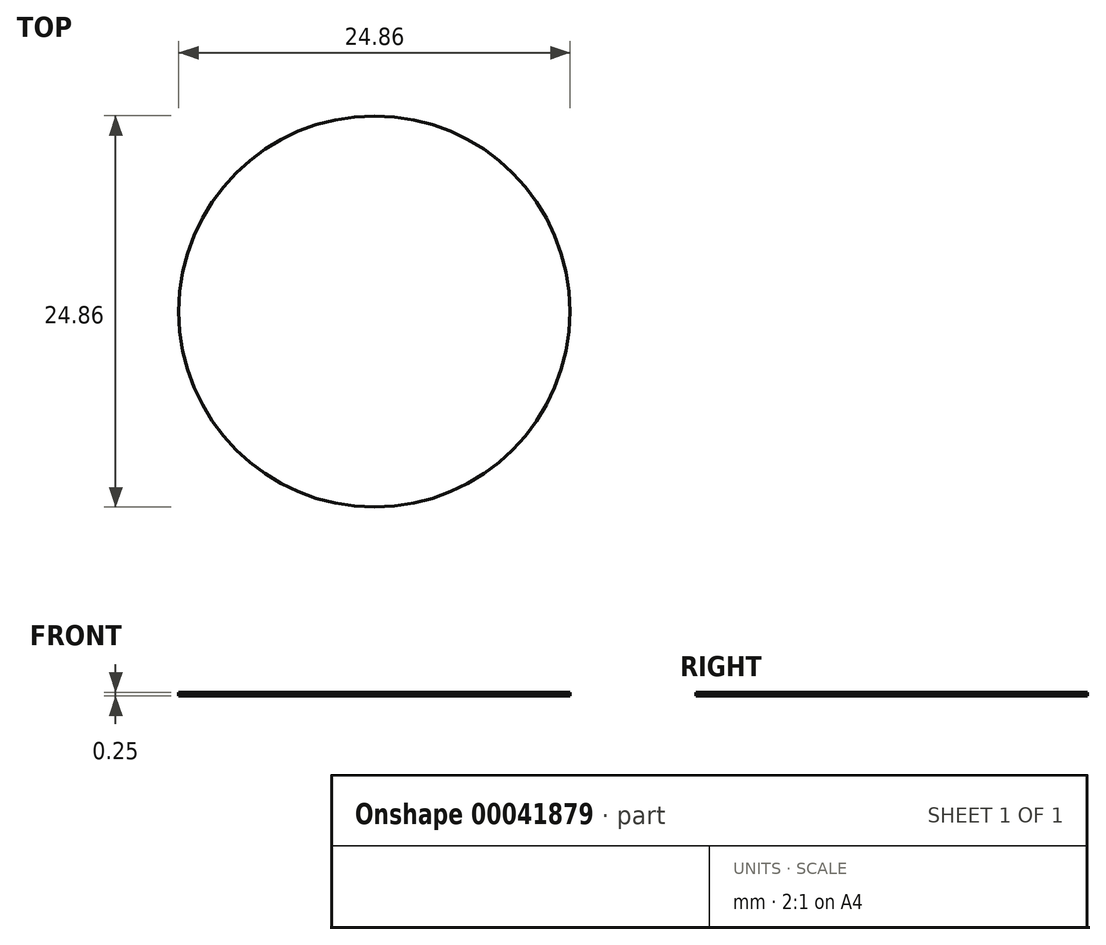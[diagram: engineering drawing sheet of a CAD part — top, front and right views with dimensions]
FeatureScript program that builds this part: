
annotation { "Feature Type Name" : "Feature", "Feature Type Description" : "" }
export const myFeature = defineFeature(function(context is Context, id is Id, definition is map)
    precondition{}
    {
        {
            var Q0;
            Q0=qCreatedBy(makeId("Top.planeOp"),FACE);
            var sketch = newSketch(context, id + "F0", { "sketchPlane" : qUnion([Q0])});
            skCircle(sketch, "E0", {"center": v(0, 0) * mm, "radius": 12.43 * mm});
            skSolve(sketch);
        }
        {
            var Q0;
            Q0=qSketchRegion(id+"F0",true);
            extrude(context, id + "F1", {"entities" : qUnion([Q0]), "depth" : .25 * mm});
        }
    });
